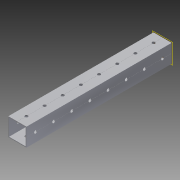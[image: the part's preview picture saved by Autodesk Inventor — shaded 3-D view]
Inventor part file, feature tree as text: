
AUTODESK INVENTOR PART (.ipt)
format: ipt  version: 2014 (Build 180170000, 170)  size: 1,162,240 bytes
history: native  units: in
note: dims shown in document units (in); Inventor stores cm internally (conversion verified against a paired STEP export)
features: pattern_circular x1, other x1, plane x1, extrude x1, imported_body x1, sketch x1
ambient origin geometry x8: Origin, YZ Plane, XZ Plane, XY Plane, X Axis, Y Axis, Z Axis, Center Point
bodies: Body1 (feature_tree)
feature tree (6):
  pattern_circular  "CirPattern2"
  other  "217-3426-STEP1"
  plane  "Work Plane1"
  extrude  "Extrusion1"  Depth=3937.0079in TaperAngle=0.0deg
  imported_body  "Base1"
  sketch  "Sketch1"  dims[d0=-5.0in d1=3937.0079in d2=0.0in]
